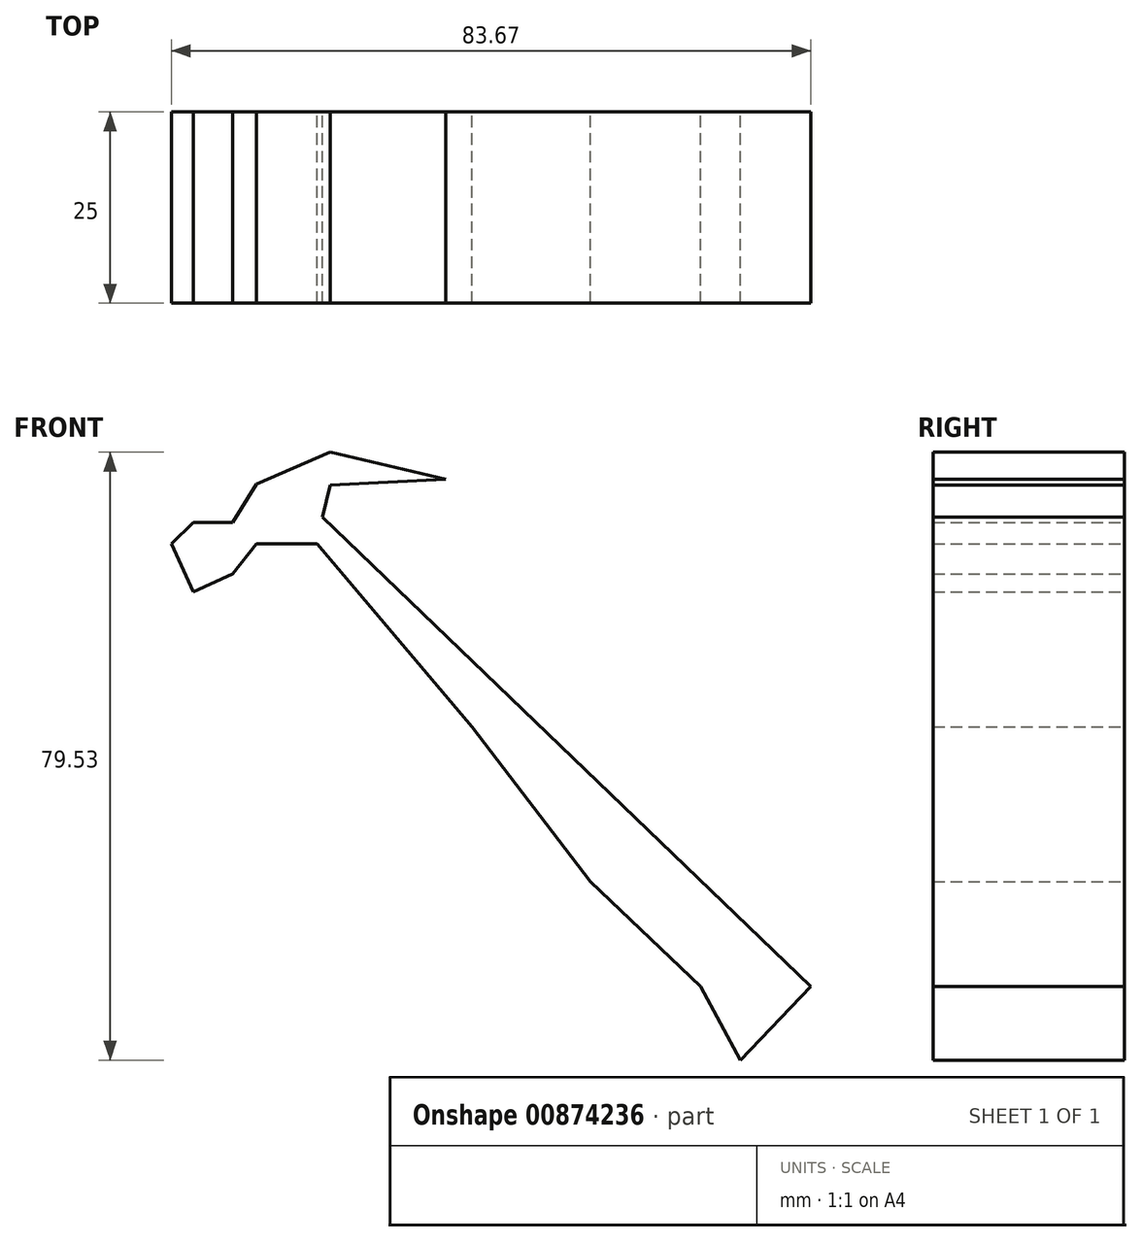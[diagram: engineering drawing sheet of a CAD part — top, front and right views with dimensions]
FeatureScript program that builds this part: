
annotation { "Feature Type Name" : "Feature", "Feature Type Description" : "" }
export const myFeature = defineFeature(function(context is Context, id is Id, definition is map)
    precondition{}
    {
        {
            var Q0;
            Q0=qCreatedBy(makeId("Front.planeOp"),FACE);
            var sketch = newSketch(context, id + "F0", { "sketchPlane" : qUnion([Q0])});
            skLineSegment(sketch, "E0", {"start": v(-7.17, 66.38) * mm, "end": v(-22.3, 69.92) * mm});
            skLineSegment(sketch, "E1", {"start": v(-22.3, 69.92) * mm, "end": v(-31.94, 65.77) * mm});
            skLineSegment(sketch, "E2", {"start": v(-31.94, 65.77) * mm, "end": v(-35.04, 60.75) * mm});
            skLineSegment(sketch, "E3", {"start": v(-35.04, 60.75) * mm, "end": v(-40.2, 60.75) * mm});
            skLineSegment(sketch, "E4", {"start": v(-40.2, 60.75) * mm, "end": v(-43.08, 57.92) * mm});
            skLineSegment(sketch, "E5", {"start": v(-43.08, 57.92) * mm, "end": v(-40.2, 51.64) * mm});
            skLineSegment(sketch, "E6", {"start": v(-40.2, 51.64) * mm, "end": v(-35.04, 54.01) * mm});
            skLineSegment(sketch, "E7", {"start": v(-35.04, 54.01) * mm, "end": v(-31.94, 57.92) * mm});
            skLineSegment(sketch, "E8", {"start": v(-31.94, 57.92) * mm, "end": v(-24.03, 57.92) * mm});
            skLineSegment(sketch, "E9", {"start": v(-24.03, 57.92) * mm, "end": v(-3.73, 34) * mm});
            skLineSegment(sketch, "E10", {"start": v(-3.73, 34) * mm, "end": v(11.75, 13.7) * mm});
            skLineSegment(sketch, "E11", {"start": v(11.75, 13.7) * mm, "end": v(26.2, 0) * mm});
            skLineSegment(sketch, "E12", {"start": v(26.2, 0) * mm, "end": v(31.35, -9.6) * mm});
            skLineSegment(sketch, "E13", {"start": v(31.35, -9.6) * mm, "end": v(40.59, 0) * mm});
            skLineSegment(sketch, "E14", {"start": v(40.59, 0) * mm, "end": v(-23.3, 61.41) * mm});
            skLineSegment(sketch, "E15", {"start": v(-23.3, 61.41) * mm, "end": v(-22.3, 65.63) * mm});
            skLineSegment(sketch, "E16", {"start": v(-22.3, 65.63) * mm, "end": v(-7.17, 66.38) * mm});
            skSolve(sketch);
        }
        {
            var Q0;
            Q0=makeQuery(id+"F0.imprint","IMPRINT",FACE,{"disambiguationData":[TD([[makeQuery(id+"F0.imprint","IMPRINT",EDGE,{"derivedFrom":sQuery(id+"F0.wireOp",EDGE,"E0")}),1.0]])]});
            extrude(context, id + "F1", {"entities" : qUnion([Q0]), "depth" : 25 * mm, "offsetDistance" : 25 * mm});
        }
    });
